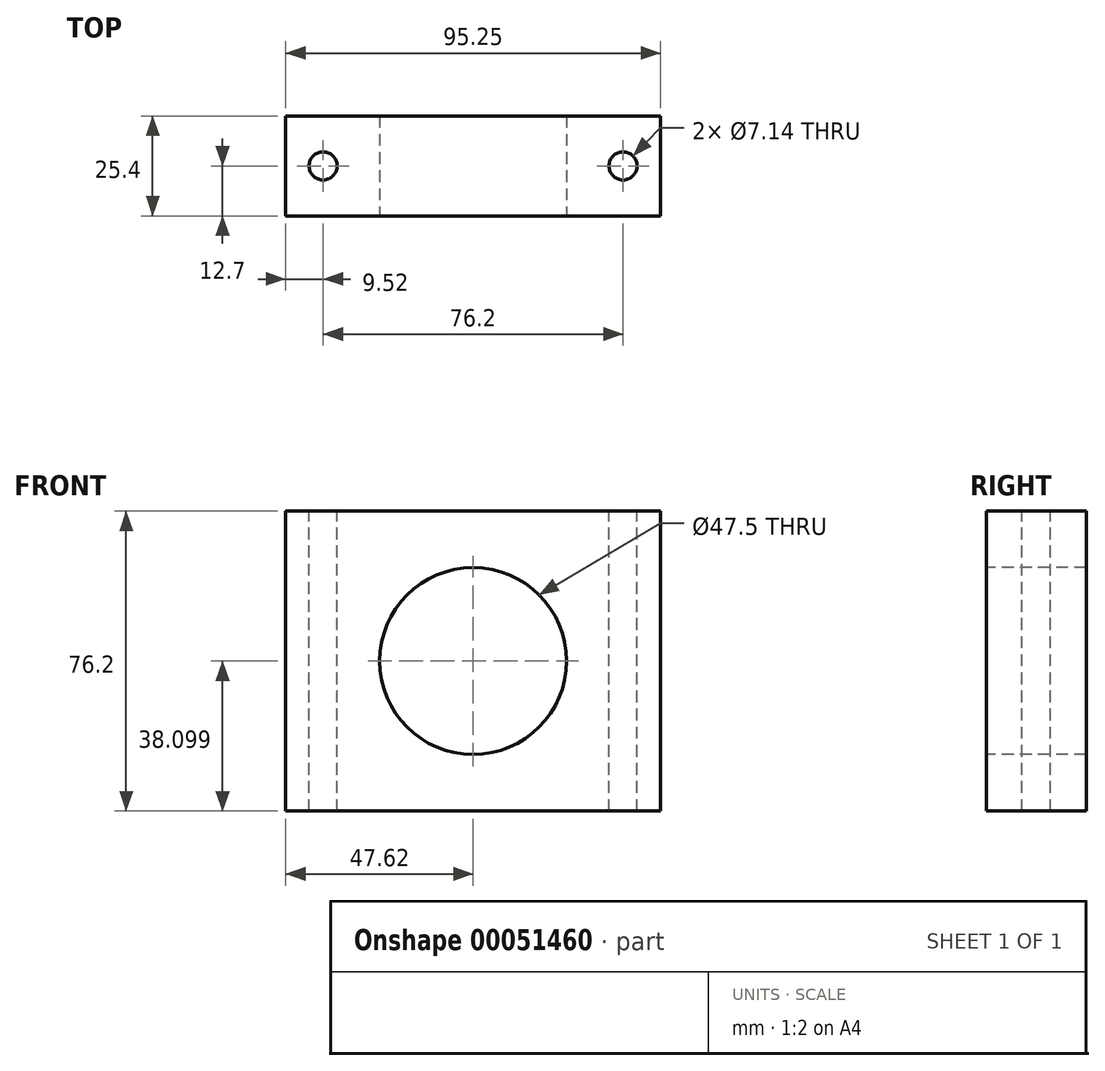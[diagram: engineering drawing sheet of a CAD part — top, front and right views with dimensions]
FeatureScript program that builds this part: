
annotation { "Feature Type Name" : "Feature", "Feature Type Description" : "" }
export const myFeature = defineFeature(function(context is Context, id is Id, definition is map)
    precondition{}
    {
        {
            var Q0;
            Q0=qCreatedBy(makeId("Front.planeOp"),FACE);
            var sketch = newSketch(context, id + "F0", { "sketchPlane" : qUnion([Q0])});
            skLineSegment(sketch, "E0.bottom", {"start": v(-32.05, 41.79) * mm, "end": v(-127.3, 41.79) * mm});
            skLineSegment(sketch, "E0.top", {"start": v(-32.05, -34.41) * mm, "end": v(-127.3, -34.41) * mm});
            skLineSegment(sketch, "E0.left", {"start": v(-32.05, 41.79) * mm, "end": v(-32.05, -34.41) * mm});
            skLineSegment(sketch, "E0.right", {"start": v(-127.3, 41.79) * mm, "end": v(-127.3, -34.41) * mm});
            skSolve(sketch);
        }
        {
            var Q0;
            Q0 = qSketchRegion(id + "F0", true);
            extrude(context, id + "F1", {"entities" : qUnion([Q0]), "depth" : 25.4 * mm});
        }
        {
            var Q0;
            Q0=makeQuery(id+"F1.opExtrude","CAP_FACE",FACE,{"disambiguationData":[OSD([sQuery(id+"F0.wireOp",EDGE,"E0.bottom"),sQuery(id+"F0.wireOp",EDGE,"E0.top"),sQuery(id+"F0.wireOp",EDGE,"E0.left"),sQuery(id+"F0.wireOp",EDGE,"E0.right")])],"isStart":false});
            var sketch = newSketch(context, id + "F2", { "sketchPlane" : qUnion([Q0])});
            skLineSegment(sketch, "E1.0", {"start": v(-79.8, 41.79) * mm, "end": v(-79.8, -34.41) * mm, "construction": true});
            skLineSegment(sketch, "E2", {"start": v(-127.3, 3.69) * mm, "end": v(-32.05, 3.69) * mm, "construction": true});
            skCircle(sketch, "E3", {"center": v(-79.68, 3.69) * mm, "radius": 23.75 * mm});
            skSolve(sketch);
        }
        {
            var Q0;
            Q0 = qSketchRegion(id + "F2", true);
            extrude(context, id + "F3", {"entities" : qUnion([Q0]), "operationType" : NewBodyOperationType.REMOVE, "oppositeDirection" : true, "depth" : 25.4 * mm});
        }
        {
            var Q0;
            Q0=makeQuery(id+"F1.opExtrude","SWEPT_FACE",FACE,{"disambiguationData":[OSD([sQuery(id+"F0.wireOp",EDGE,"E0.bottom")])]});
            var sketch = newSketch(context, id + "F4", { "sketchPlane" : qUnion([Q0])});
            skLineSegment(sketch, "E4.0", {"start": v(-41.58, -25.4) * mm, "end": v(-41.58, 0) * mm, "construction": true});
            skCircle(sketch, "E5", {"center": v(-41.58, -12.7) * mm, "radius": 3.57 * mm});
            skLineSegment(sketch, "E6", {"start": v(-79.68, 0) * mm, "end": v(-79.68, -25.4) * mm, "construction": true});
            skLineSegment(sketch, "E7.MirrorCS", {"start": v(-117.78, -25.4) * mm, "end": v(-117.78, 0) * mm, "construction": true});
            skCircle(sketch, "E8", {"center": v(-117.78, -12.7) * mm, "radius": 3.57 * mm});
            skSolve(sketch);
        }
        {
            var Q0;
            Q0 = qSketchRegion(id + "F4", true);
            extrude(context, id + "F5", {"entities" : qUnion([Q0]), "operationType" : NewBodyOperationType.REMOVE, "endBound" : BoundingType.THROUGH_ALL, "oppositeDirection" : true, "depth" : 25.4 * mm});
        }
    });
